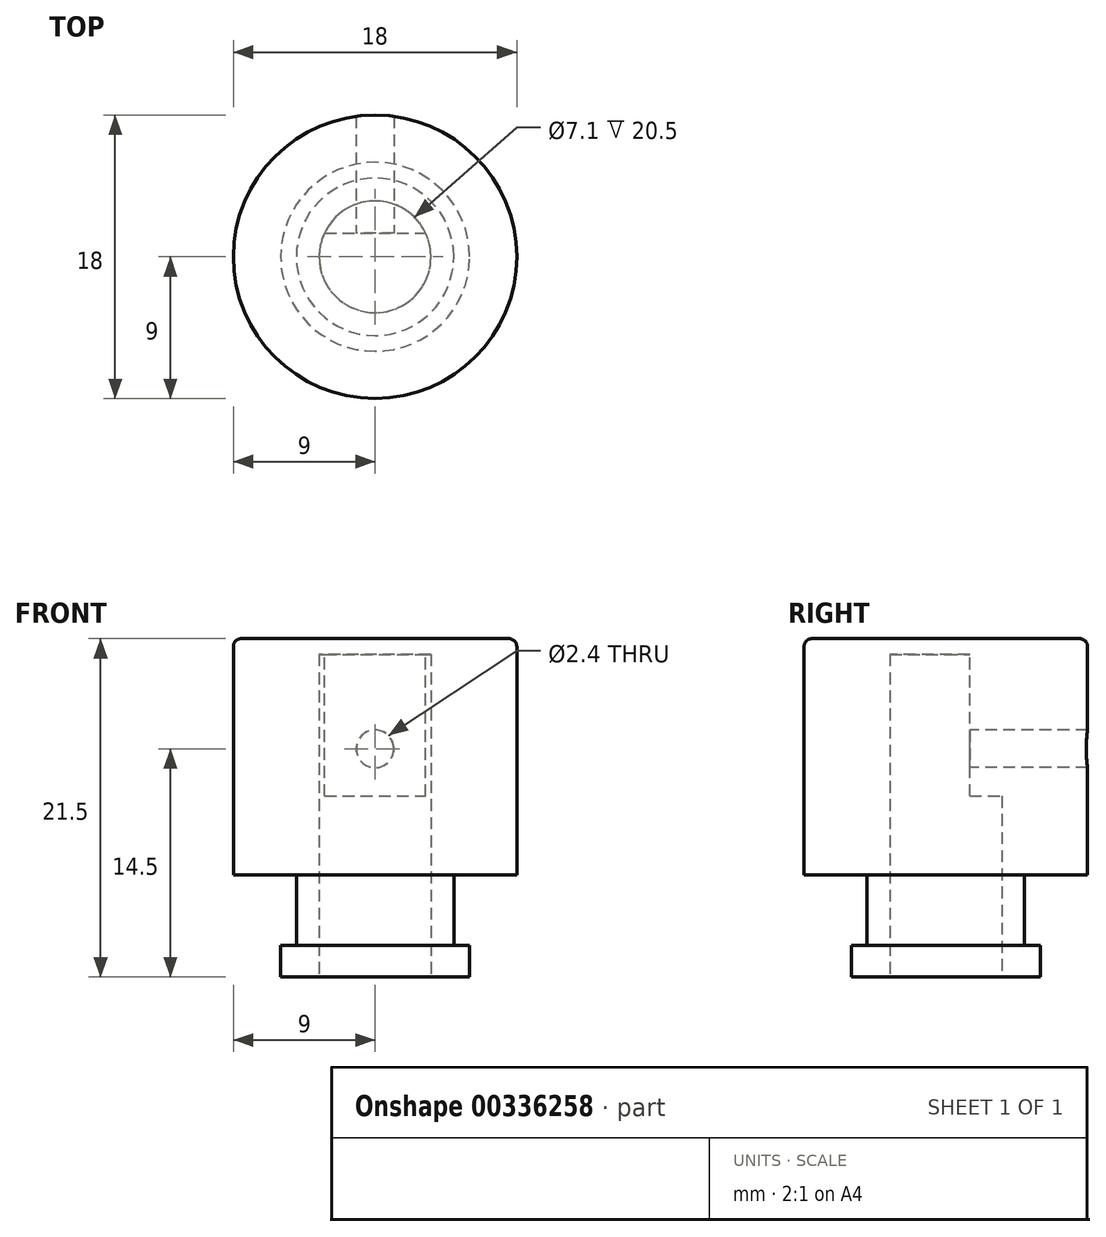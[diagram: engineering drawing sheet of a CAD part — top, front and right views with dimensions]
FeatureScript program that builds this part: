
annotation { "Feature Type Name" : "Feature", "Feature Type Description" : "" }
export const myFeature = defineFeature(function(context is Context, id is Id, definition is map)
    precondition{}
    {
        {
            var Q0;
            Q0=qCreatedBy(makeId("Front.planeOp"),FACE);
            var sketch = newSketch(context, id + "F0", { "sketchPlane" : qUnion([Q0])});
            skLineSegment(sketch, "E0", {"start": v(0, -2.23) * mm, "end": v(0, -5.1) * mm, "construction": true});
            skLineSegment(sketch, "E1", {"start": v(0, 0) * mm, "end": v(-6, 0) * mm});
            skLineSegment(sketch, "E2", {"start": v(-6, 0) * mm, "end": v(-6, 2) * mm});
            skLineSegment(sketch, "E3", {"start": v(-6, 2) * mm, "end": v(-5, 2) * mm});
            skLineSegment(sketch, "E4", {"start": v(-5, 2) * mm, "end": v(-5, 6.5) * mm});
            skLineSegment(sketch, "E5", {"start": v(-5, 6.5) * mm, "end": v(-9, 6.5) * mm});
            skLineSegment(sketch, "E6", {"start": v(-9, 6.5) * mm, "end": v(-9, 21.5) * mm});
            skLineSegment(sketch, "E7", {"start": v(-9, 21.5) * mm, "end": v(0, 21.5) * mm});
            skLineSegment(sketch, "E8", {"start": v(0, 0) * mm, "end": v(0, 21.5) * mm});
            skSolve(sketch);
        }
        {
            var Q0;
            Q0 = qSketchRegion(id + "F0", true);
            var Q1;
            Q1=sQuery(id+"F0.wireOp",EDGE,"E0");
            revolve(context, id + "F1", {"entities" : qUnion([Q0]), "axis" : qUnion([Q1]), "revolveType" : RevolveType.FULL});
        }
        {
            var Q0;
            Q0=makeQuery(id+"F1.opRevolve","SWEPT_FACE",FACE,{"disambiguationData":[OSD([sQuery(id+"F0.wireOp",EDGE,"E1")])]});
            var sketch = newSketch(context, id + "F2", { "sketchPlane" : qUnion([Q0])});
            skCircle(sketch, "E9", {"center": v(0, 0) * mm, "radius": 3.55 * mm});
            skSolve(sketch);
        }
        {
            var Q0;
            Q0 = qSketchRegion(id + "F2", true);
            extrude(context, id + "F3", {"entities" : qUnion([Q0]), "operationType" : NewBodyOperationType.REMOVE, "oppositeDirection" : true, "depth" : 20.5 * mm});
        }
        {
            var Q0;
            Q0=makeQuery(id+"F3.boolean.opBoolean","COPY",FACE,{"derivedFrom":makeQuery(id+"F3.opExtrude","CAP_FACE",FACE,{"disambiguationData":[OSD([sQuery(id+"F2.wireOp",EDGE,"E9")])],"isStart":false})});
            var sketch = newSketch(context, id + "F4", { "sketchPlane" : qUnion([Q0])});
            skArc(sketch, "E10", {"start": v(-3.2, -1.52) * mm, "mid": v(0, -3.55) * mm, "end": v(3.2, -1.52) * mm});
            skLineSegment(sketch, "E11", {"start": v(-3.2, -1.52) * mm, "end": v(3.2, -1.52) * mm});
            skSolve(sketch);
        }
        {
            var Q0;
            Q0 = qSketchRegion(id + "F4", true);
            extrude(context, id + "F5", {"entities" : qUnion([Q0]), "operationType" : NewBodyOperationType.ADD, "depth" : 9 * mm});
        }
        {
            var Q0;
            Q0=makeQuery(id+"F1.opRevolve","SWEPT_EDGE",EDGE,{"disambiguationData":[OSD([sQuery(id+"F0.wireOp",EDGE,"E6"),sQuery(id+"F0.wireOp",EDGE,"E7")])]});
            fillet(context, id + "F6", {"entities" : qUnion([Q0]), "radius" : 0.5 * mm, "tangentPropagation" : true, "allowEdgeOverflow" : false});
        }
        {
            var Q0;
            Q0=makeQuery(id+"F5.opExtrude","SWEPT_FACE",FACE,{"disambiguationData":[OSD([sQuery(id+"F4.wireOp",EDGE,"E11")])]});
            var sketch = newSketch(context, id + "F7", { "sketchPlane" : qUnion([Q0])});
            skCircle(sketch, "E12", {"center": v(0, 14.5) * mm, "radius": 1.2 * mm});
            skPoint(sketch, "E12.centerSnap0", {"position": v(0, 11.5) * mm});
            skSolve(sketch);
        }
        {
            var Q0;
            Q0 = qSketchRegion(id + "F7", true);
            extrude(context, id + "F8", {"entities" : qUnion([Q0]), "operationType" : NewBodyOperationType.REMOVE, "oppositeDirection" : true, "depth" : 25 * mm});
        }
    });
